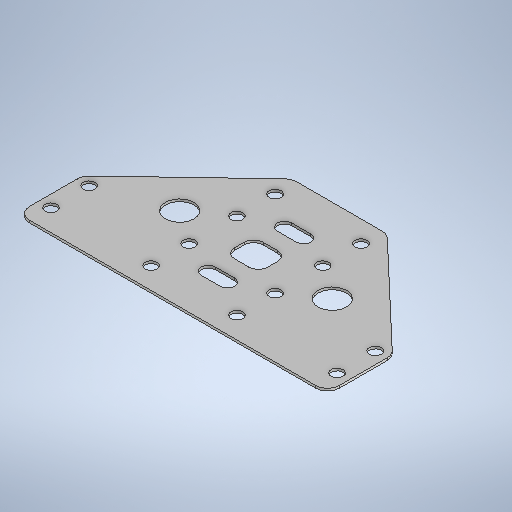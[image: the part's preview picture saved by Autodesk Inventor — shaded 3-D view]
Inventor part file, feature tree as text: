
AUTODESK INVENTOR PART (.ipt)
format: ipt  version: 2025.1 (Build 291241000, 241)  size: 341,504 bytes
history: native  units: mm
features: sketch x5, extrude x3, fillet x3, hole x3, mirror x2, plane x1
ambient origin geometry x8: Origin, YZ Plane, XZ Plane, XY Plane, X Axis, Y Axis, Z Axis, Center Point
bodies: Solid1 (feature_tree)
feature tree (17):
  extrude  "Extrusion1"  Depth=65.0mm
  fillet  "Fillet1"  Radius=35.0mm
  sketch  "Sketch2"  dims[d3=20.0mm d4=0.5mm d5=0.0mm]
  hole  "Hole1"  [1 undecoded]
  hole  "Hole2"  [1 undecoded]
  extrude  "Extrusion2"  Depth=8.0mm
  fillet  "Fillet2"  Radius=8.0mm
  extrude  "Extrusion3"  Depth=2.5mm
  plane  "Work Plane1"
  mirror  "Mirror1"
  hole  "Hole3"  [1 undecoded]
  mirror  "Mirror2"
  fillet  "Fillet3"  Radius=7.0mm
  sketch  "Sketch1"  dims[d0=13.6mm d1=65.0mm d2=35.0mm]
  sketch  "Sketch3"  dims[d6=2.5mm d9=60.0mm]
  sketch  "Sketch4"  dims[d10=30.0mm d11=4.5mm d12=8.0mm]
  sketch  "Sketch5"  dims[d13=16.0mm d14=32.0mm d15=5.0mm d16=6.0mm d17=8.0mm d18=4.0mm d19=2.0mm d20=90.0deg d21=8.0mm d22=0.0mm d23=2.5mm d24=6.0mm d25=4.0mm d26=2.0mm d27=90.0deg d28=8.0mm d29=0.0mm d30=7.0mm d31=6.0mm d32=0.5mm d33=0.0mm d34=2.0mm d35=1.5mm d37=4.0mm d39=3.0mm d40=2.0mm d41=10.0mm d42=0.0mm d43=-17.5mm d44=18.0mm d45=9.0mm d46=4.5mm d47=2.5mm d48=6.0mm d49=4.0mm d50=2.0mm d51=90.0deg d52=8.0mm d53=0.0mm d54=2.5mm]
note: 3 required parameter values undecoded (feature->parameter linkage not recoverable at this tier; creation-order binding heuristic only, values carry confidence <= 0.55)
